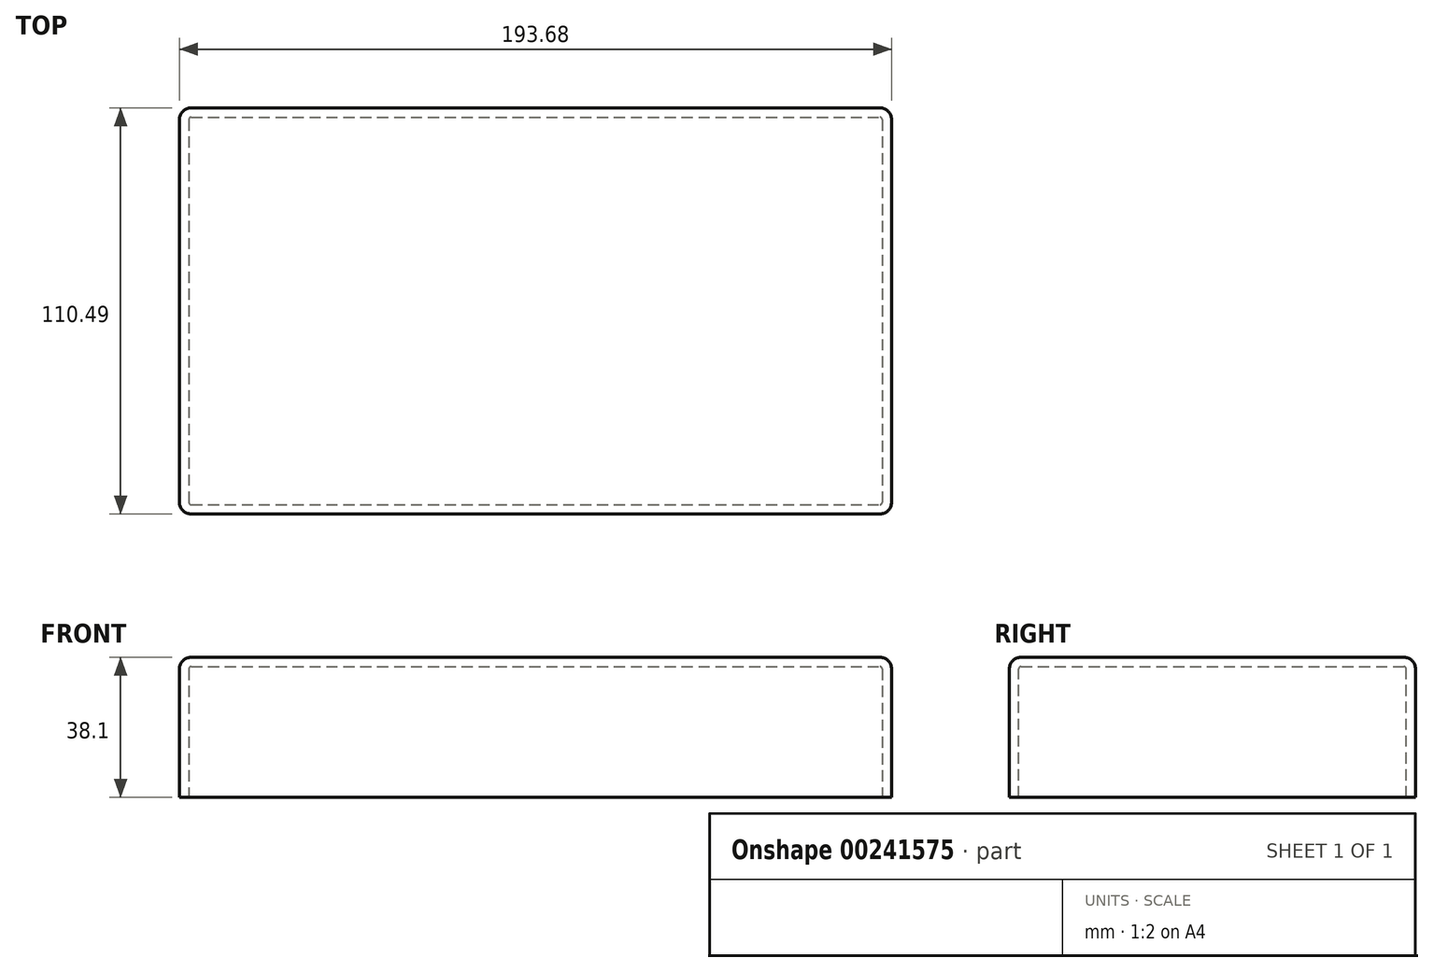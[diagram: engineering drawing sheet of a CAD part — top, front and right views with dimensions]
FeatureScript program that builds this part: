
annotation { "Feature Type Name" : "Feature", "Feature Type Description" : "" }
export const myFeature = defineFeature(function(context is Context, id is Id, definition is map)
    precondition{}
    {
        {
            var Q0;
            Q0=qCreatedBy(makeId("Top.planeOp"),FACE);
            var sketch = newSketch(context, id + "F0", { "sketchPlane" : qUnion([Q0])});
            skLineSegment(sketch, "E0.bottom", {"start": v(-116.16, 63.41) * mm, "end": v(77.52, 63.41) * mm});
            skLineSegment(sketch, "E0.top", {"start": v(-116.16, -47.08) * mm, "end": v(77.52, -47.08) * mm});
            skLineSegment(sketch, "E0.left", {"start": v(-116.16, 63.41) * mm, "end": v(-116.16, -47.08) * mm});
            skLineSegment(sketch, "E0.right", {"start": v(77.52, 63.41) * mm, "end": v(77.52, -47.08) * mm});
            skSolve(sketch);
        }
        {
            var Q0;
            Q0=makeQuery(id+"F0.imprint","IMPRINT",FACE,{"disambiguationData":[TD([[makeQuery(id+"F0.imprint","IMPRINT",EDGE,{"derivedFrom":sQuery(id+"F0.wireOp",EDGE,"E0.bottom")}),-1.0]])]});
            extrude(context, id + "F1", {"entities" : qUnion([Q0]), "depth" : 38.1 * mm});
        }
        {
            var Q0;
            Q0=makeQuery(id+"F1.opExtrude","CAP_EDGE",EDGE,{"disambiguationData":[OSD([sQuery(id+"F0.wireOp",EDGE,"E0.left")])],"isStart":false});
            var Q1;
            Q1=makeQuery(id+"F1.opExtrude","CAP_EDGE",EDGE,{"disambiguationData":[OSD([sQuery(id+"F0.wireOp",EDGE,"E0.bottom")])],"isStart":false});
            var Q2;
            Q2=makeQuery(id+"F1.opExtrude","CAP_EDGE",EDGE,{"disambiguationData":[OSD([sQuery(id+"F0.wireOp",EDGE,"E0.top")])],"isStart":false});
            var Q3;
            Q3=makeQuery(id+"F1.opExtrude","CAP_EDGE",EDGE,{"disambiguationData":[OSD([sQuery(id+"F0.wireOp",EDGE,"E0.right")])],"isStart":false});
            var Q4;
            Q4=makeQuery(id+"F1.opExtrude","SWEPT_EDGE",EDGE,{"disambiguationData":[OSD([sQuery(id+"F0.wireOp",EDGE,"E0.bottom"),sQuery(id+"F0.wireOp",EDGE,"E0.right")])]});
            var Q5;
            Q5=makeQuery(id+"F1.opExtrude","SWEPT_EDGE",EDGE,{"disambiguationData":[OSD([sQuery(id+"F0.wireOp",EDGE,"E0.top"),sQuery(id+"F0.wireOp",EDGE,"E0.right")])]});
            var Q6;
            Q6=makeQuery(id+"F1.opExtrude","SWEPT_EDGE",EDGE,{"disambiguationData":[OSD([sQuery(id+"F0.wireOp",EDGE,"E0.top"),sQuery(id+"F0.wireOp",EDGE,"E0.left")])]});
            var Q7;
            Q7=makeQuery(id+"F1.opExtrude","SWEPT_EDGE",EDGE,{"disambiguationData":[OSD([sQuery(id+"F0.wireOp",EDGE,"E0.bottom"),sQuery(id+"F0.wireOp",EDGE,"E0.left")])]});
            fillet(context, id + "F2", {"entities" : qUnion([Q0, Q1, Q2, Q3, Q4, Q5, Q6, Q7]), "radius" : 3.17 * mm, "tangentPropagation" : true, "allowEdgeOverflow" : false});
        }
        {
            var Q0;
            Q0=makeQuery(id+"F1.opExtrude","CAP_FACE",FACE,{"disambiguationData":[OSD([sQuery(id+"F0.wireOp",EDGE,"E0.bottom"),sQuery(id+"F0.wireOp",EDGE,"E0.top"),sQuery(id+"F0.wireOp",EDGE,"E0.left"),sQuery(id+"F0.wireOp",EDGE,"E0.right")])],"isStart":true});
            shell(context, id + "F3", {"entities" : qUnion([Q0]), "thickness" : 2.54 * mm});
        }
    });
